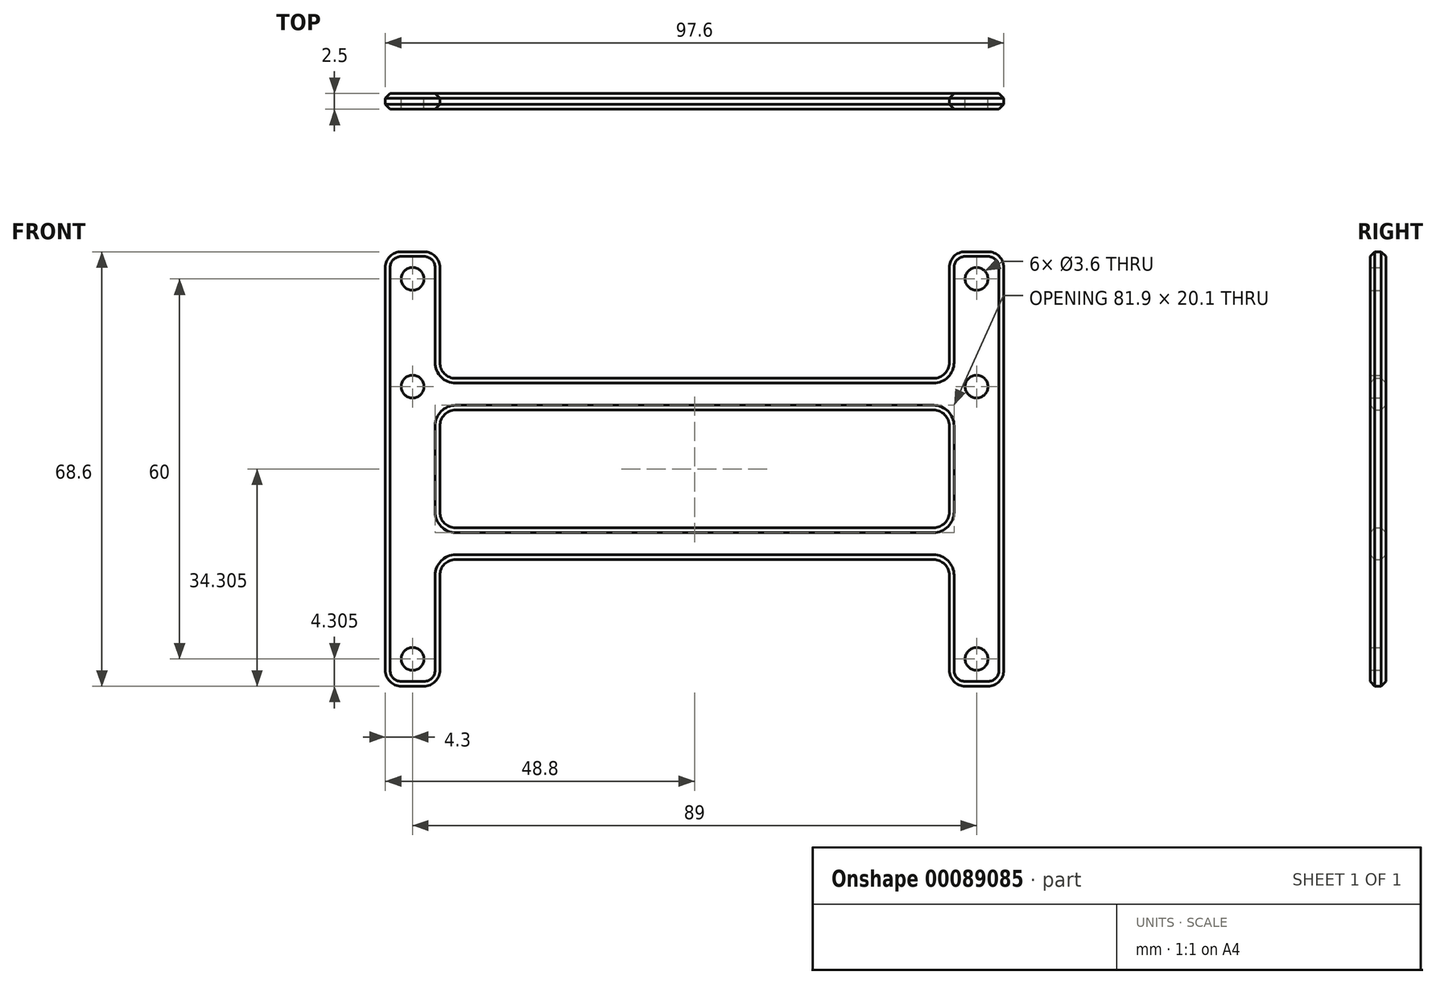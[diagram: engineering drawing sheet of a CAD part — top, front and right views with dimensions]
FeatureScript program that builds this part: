
annotation { "Feature Type Name" : "Feature", "Feature Type Description" : "" }
export const myFeature = defineFeature(function(context is Context, id is Id, definition is map)
    precondition{}
    {
        {
            var Q0;
            Q0=qCreatedBy(makeId("Front.planeOp"),FACE);
            var sketch = newSketch(context, id + "F0", { "sketchPlane" : qUnion([Q0])});
            skLineSegment(sketch, "E0.bottom", {"start": v(-48.8, 64.62) * mm, "end": v(-40.2, 64.62) * mm});
            skLineSegment(sketch, "E0.top", {"start": v(-48.8, -3.98) * mm, "end": v(-40.2, -3.98) * mm});
            skLineSegment(sketch, "E0.left", {"start": v(-48.8, 64.62) * mm, "end": v(-48.8, -3.98) * mm});
            skLineSegment(sketch, "E1", {"start": v(-44.5, 64.62) * mm, "end": v(-44.5, -55.68) * mm, "construction": true});
            skCircle(sketch, "E2", {"center": v(-44.5, 60.32) * mm, "radius": 1.8 * mm});
            skCircle(sketch, "E3", {"center": v(-44.5, 43.33) * mm, "radius": 1.8 * mm});
            skCircle(sketch, "E4", {"center": v(-44.5, 0.32) * mm, "radius": 1.8 * mm});
            skLineSegment(sketch, "E5", {"start": v(-40.2, 64.62) * mm, "end": v(-40.2, -3.98) * mm});
            skLineSegment(sketch, "E6.bottom", {"start": v(-40.2, 44.62) * mm, "end": v(0, 44.62) * mm});
            skLineSegment(sketch, "E6.top", {"start": v(-40.2, 39.62) * mm, "end": v(0, 39.62) * mm});
            skLineSegment(sketch, "E6.left", {"start": v(-40.2, 44.62) * mm, "end": v(-40.2, 39.62) * mm});
            skLineSegment(sketch, "E6.right", {"start": v(0, 44.62) * mm, "end": v(0, 39.62) * mm});
            skLineSegment(sketch, "E7.bottom", {"start": v(-40.23, 21.03) * mm, "end": v(0, 21.02) * mm});
            skLineSegment(sketch, "E7.top", {"start": v(-40.23, 16.03) * mm, "end": v(0, 16.02) * mm});
            skLineSegment(sketch, "E7.left", {"start": v(-40.23, 21.03) * mm, "end": v(-40.23, 16.02) * mm});
            skLineSegment(sketch, "E7.right", {"start": v(0, 21.02) * mm, "end": v(0, 16.02) * mm});
            skLineSegment(sketch, "E8.MirrorCS", {"start": v(40.23, 21.03) * mm, "end": v(40.23, 16.02) * mm});
            skCircle(sketch, "E9.MirrorC", {"center": v(44.5, 43.33) * mm, "radius": 1.8 * mm});
            skLineSegment(sketch, "E10.MirrorCS", {"start": v(40.2, 44.62) * mm, "end": v(40.2, 39.62) * mm});
            skLineSegment(sketch, "E11.MirrorCS", {"start": v(40.23, 16.02) * mm, "end": v(0, 16.02) * mm});
            skLineSegment(sketch, "E12.MirrorCS", {"start": v(40.23, 21.02) * mm, "end": v(0, 21.02) * mm});
            skCircle(sketch, "E13.MirrorC", {"center": v(44.5, 0.32) * mm, "radius": 1.8 * mm});
            skCircle(sketch, "E14.MirrorC", {"center": v(44.5, 60.32) * mm, "radius": 1.8 * mm});
            skLineSegment(sketch, "E15.MirrorCS", {"start": v(40.2, 39.62) * mm, "end": v(0, 39.62) * mm});
            skLineSegment(sketch, "E16.MirrorCS", {"start": v(48.8, 64.62) * mm, "end": v(48.8, -3.98) * mm});
            skLineSegment(sketch, "E17.MirrorCS", {"start": v(48.8, -3.98) * mm, "end": v(40.2, -3.98) * mm});
            skLineSegment(sketch, "E18.MirrorCS", {"start": v(40.2, 64.62) * mm, "end": v(40.2, -3.97) * mm});
            skLineSegment(sketch, "E19.MirrorCS", {"start": v(48.8, 64.62) * mm, "end": v(40.2, 64.62) * mm});
            skLineSegment(sketch, "E20.MirrorCS", {"start": v(40.2, 44.62) * mm, "end": v(0, 44.62) * mm});
            skSolve(sketch);
        }
        {
            var Q0;
            {var subQ5=sQuery(id+"F0.wireOp",EDGE,"E7.left");Q0=makeQuery(id+"F0.imprint","IMPRINT",FACE,{"disambiguationData":[TD([[makeQuery(id+"F0.imprint","IMPRINT",EDGE,{"derivedFrom":subQ5}),1.0]])]});}
            var Q1;
            {var subQ0=sQuery(id+"F0.wireOp",EDGE,"E8.MirrorCS");Q1=makeQuery(id+"F0.imprint","IMPRINT",FACE,{"disambiguationData":[TD([[makeQuery(id+"F0.imprint","IMPRINT",EDGE,{"derivedFrom":subQ0}),-1.0]])]});}
            var Q2;
            {var subQ5=sQuery(id+"F0.wireOp",EDGE,"E7.right");Q2=makeQuery(id+"F0.imprint","IMPRINT",FACE,{"disambiguationData":[TD([[makeQuery(id+"F0.imprint","IMPRINT",EDGE,{"derivedFrom":subQ5}),-1.0]])]});}
            var Q3;
            {var subQ0=sQuery(id+"F0.wireOp",EDGE,"E7.right");Q3=makeQuery(id+"F0.imprint","IMPRINT",FACE,{"disambiguationData":[TD([[makeQuery(id+"F0.imprint","IMPRINT",EDGE,{"derivedFrom":subQ0}),1.0]])]});}
            var Q4;
            {var subQ0=sQuery(id+"F0.wireOp",EDGE,"E15.MirrorCS");Q4=makeQuery(id+"F0.imprint","IMPRINT",FACE,{"disambiguationData":[TD([[makeQuery(id+"F0.imprint","IMPRINT",EDGE,{"derivedFrom":subQ0}),-1.0]])]});}
            var Q5;
            {var subQ9=sQuery(id+"F0.wireOp",EDGE,"E8.MirrorCS");Q5=makeQuery(id+"F0.imprint","IMPRINT",FACE,{"disambiguationData":[TD([[makeQuery(id+"F0.imprint","IMPRINT",EDGE,{"derivedFrom":subQ9}),1.0]])]});}
            var Q6;
            Q6=makeQuery(id+"F0.imprint","IMPRINT",FACE,{"disambiguationData":[TD([[makeQuery(id+"F0.imprint","IMPRINT",EDGE,{"derivedFrom":sQuery(id+"F0.wireOp",EDGE,"E6.bottom")}),-1.0]])]});
            var Q7;
            Q7=makeQuery(id+"F0.imprint","IMPRINT",FACE,{"disambiguationData":[TD([[makeQuery(id+"F0.imprint","IMPRINT",EDGE,{"derivedFrom":sQuery(id+"F0.wireOp",EDGE,"6060c022-7060-453b-8efb-dcd9e4211910.sketch_text.stroke-0")}),-1.0]])]});
            var Q8;
            Q8=makeQuery(id+"F0.imprint","IMPRINT",FACE,{"disambiguationData":[TD([[makeQuery(id+"F0.imprint","IMPRINT",EDGE,{"derivedFrom":sQuery(id+"F0.wireOp",EDGE,"6060c022-7060-453b-8efb-dcd9e4211910.sketch_text.stroke-80")}),-1.0]])]});
            var Q9;
            Q9=makeQuery(id+"F0.imprint","IMPRINT",FACE,{"disambiguationData":[TD([[makeQuery(id+"F0.imprint","IMPRINT",EDGE,{"derivedFrom":sQuery(id+"F0.wireOp",EDGE,"6060c022-7060-453b-8efb-dcd9e4211910.sketch_text.stroke-109")}),1.0]])]});
            var Q10;
            Q10=makeQuery(id+"F0.imprint","IMPRINT",FACE,{"disambiguationData":[TD([[makeQuery(id+"F0.imprint","IMPRINT",EDGE,{"derivedFrom":sQuery(id+"F0.wireOp",EDGE,"6060c022-7060-453b-8efb-dcd9e4211910.sketch_text.stroke-75")}),1.0]])]});
            var Q11;
            Q11=makeQuery(id+"F0.imprint","IMPRINT",FACE,{"disambiguationData":[TD([[makeQuery(id+"F0.imprint","IMPRINT",EDGE,{"derivedFrom":sQuery(id+"F0.wireOp",EDGE,"6060c022-7060-453b-8efb-dcd9e4211910.sketch_text.stroke-56")}),1.0]])]});
            var Q12;
            Q12=makeQuery(id+"F0.imprint","IMPRINT",FACE,{"disambiguationData":[TD([[makeQuery(id+"F0.imprint","IMPRINT",EDGE,{"derivedFrom":sQuery(id+"F0.wireOp",EDGE,"6060c022-7060-453b-8efb-dcd9e4211910.sketch_text.stroke-23")}),-1.0]])]});
            var Q13;
            Q13=makeQuery(id+"F0.imprint","IMPRINT",FACE,{"disambiguationData":[TD([[makeQuery(id+"F0.imprint","IMPRINT",EDGE,{"derivedFrom":sQuery(id+"F0.wireOp",EDGE,"6060c022-7060-453b-8efb-dcd9e4211910.sketch_text.stroke-13")}),-1.0]])]});
            var Q14;
            Q14=makeQuery(id+"F0.imprint","IMPRINT",FACE,{"disambiguationData":[TD([[makeQuery(id+"F0.imprint","IMPRINT",EDGE,{"derivedFrom":sQuery(id+"F0.wireOp",EDGE,"6060c022-7060-453b-8efb-dcd9e4211910.sketch_text.stroke-8")}),1.0]])]});
            var Q15;
            Q15=makeQuery(id+"F0.imprint","IMPRINT",FACE,{"disambiguationData":[TD([[makeQuery(id+"F0.imprint","IMPRINT",EDGE,{"derivedFrom":sQuery(id+"F0.wireOp",EDGE,"6060c022-7060-453b-8efb-dcd9e4211910.sketch_text.stroke-118")}),1.0]])]});
            var Q16;
            Q16=makeQuery(id+"F0.imprint","IMPRINT",FACE,{"disambiguationData":[TD([[makeQuery(id+"F0.imprint","IMPRINT",EDGE,{"derivedFrom":sQuery(id+"F0.wireOp",EDGE,"6060c022-7060-453b-8efb-dcd9e4211910.sketch_text.stroke-136")}),-1.0]])]});
            var Q17;
            Q17=makeQuery(id+"F0.imprint","IMPRINT",FACE,{"disambiguationData":[TD([[makeQuery(id+"F0.imprint","IMPRINT",EDGE,{"derivedFrom":sQuery(id+"F0.wireOp",EDGE,"6060c022-7060-453b-8efb-dcd9e4211910.sketch_text.stroke-124")}),-1.0]])]});
            var Q18;
            Q18=makeQuery(id+"F0.imprint","IMPRINT",FACE,{"disambiguationData":[TD([[makeQuery(id+"F0.imprint","IMPRINT",EDGE,{"derivedFrom":sQuery(id+"F0.wireOp",EDGE,"6060c022-7060-453b-8efb-dcd9e4211910.sketch_text.stroke-42")}),-1.0]])]});
            var Q19;
            Q19=makeQuery(id+"F0.imprint","IMPRINT",FACE,{"disambiguationData":[TD([[makeQuery(id+"F0.imprint","IMPRINT",EDGE,{"derivedFrom":sQuery(id+"F0.wireOp",EDGE,"6060c022-7060-453b-8efb-dcd9e4211910.sketch_text.stroke-187")}),-1.0]])]});
            var Q20;
            Q20=makeQuery(id+"F0.imprint","IMPRINT",FACE,{"disambiguationData":[TD([[makeQuery(id+"F0.imprint","IMPRINT",EDGE,{"derivedFrom":sQuery(id+"F0.wireOp",EDGE,"6060c022-7060-453b-8efb-dcd9e4211910.sketch_text.stroke-61")}),-1.0]])]});
            var Q21;
            {var subQ4=sQuery(id+"F0.wireOp",EDGE,"E0.bottom");Q21=makeQuery(id+"F0.imprint","IMPRINT",FACE,{"disambiguationData":[TD([[makeQuery(id+"F0.imprint","IMPRINT",EDGE,{"derivedFrom":subQ4}),-1.0]])]});}
            var Q22;
            Q22=makeQuery(id+"F0.imprint","IMPRINT",FACE,{"disambiguationData":[TD([[makeQuery(id+"F0.imprint","IMPRINT",EDGE,{"derivedFrom":sQuery(id+"F0.wireOp",EDGE,"6060c022-7060-453b-8efb-dcd9e4211910.sketch_text.stroke-195")}),-1.0]])]});
            var Q23;
            Q23=makeQuery(id+"F0.imprint","IMPRINT",FACE,{"disambiguationData":[TD([[makeQuery(id+"F0.imprint","IMPRINT",EDGE,{"derivedFrom":sQuery(id+"F0.wireOp",EDGE,"6060c022-7060-453b-8efb-dcd9e4211910.sketch_text.stroke-155")}),-1.0]])]});
            var Q24;
            Q24=makeQuery(id+"F0.imprint","IMPRINT",FACE,{"disambiguationData":[TD([[makeQuery(id+"F0.imprint","IMPRINT",EDGE,{"derivedFrom":sQuery(id+"F0.wireOp",EDGE,"6060c022-7060-453b-8efb-dcd9e4211910.sketch_text.stroke-234")}),-1.0]])]});
            var Q25;
            Q25=makeQuery(id+"F0.imprint","IMPRINT",FACE,{"disambiguationData":[TD([[makeQuery(id+"F0.imprint","IMPRINT",EDGE,{"derivedFrom":sQuery(id+"F0.wireOp",EDGE,"6060c022-7060-453b-8efb-dcd9e4211910.sketch_text.stroke-224")}),-1.0]])]});
            var Q26;
            Q26=makeQuery(id+"F0.imprint","IMPRINT",FACE,{"disambiguationData":[TD([[makeQuery(id+"F0.imprint","IMPRINT",EDGE,{"derivedFrom":sQuery(id+"F0.wireOp",EDGE,"6060c022-7060-453b-8efb-dcd9e4211910.sketch_text.stroke-212")}),-1.0]])]});
            var Q27;
            Q27=makeQuery(id+"F0.imprint","IMPRINT",FACE,{"disambiguationData":[TD([[makeQuery(id+"F0.imprint","IMPRINT",EDGE,{"derivedFrom":sQuery(id+"F0.wireOp",EDGE,"6060c022-7060-453b-8efb-dcd9e4211910.sketch_text.stroke-216")}),-1.0]])]});
            var Q28;
            Q28=makeQuery(id+"F0.imprint","IMPRINT",FACE,{"disambiguationData":[TD([[makeQuery(id+"F0.imprint","IMPRINT",EDGE,{"derivedFrom":sQuery(id+"F0.wireOp",EDGE,"6060c022-7060-453b-8efb-dcd9e4211910.sketch_text.stroke-183")}),-1.0]])]});
            var Q29;
            Q29=qSketchRegion(id+"F0",true);
            extrude(context, id + "F1", {"entities" : qUnion([Q0, Q1, Q2, Q3, Q4, Q5, Q6, Q7, Q8, Q9, Q10, Q11, Q12, Q13, Q14, Q15, Q16, Q17, Q18, Q19, Q20, Q21, Q22, Q23, Q24, Q25, Q26, Q27, Q28, Q29]), "depth" : 2.5 * mm});
        }
        {
            var Q0;
            Q0=makeQuery(id+"F1.opExtrude","SWEPT_EDGE",EDGE,{"disambiguationData":[OSD([sQuery(id+"F0.wireOp",EDGE,"E5"),sQuery(id+"F0.wireOp",EDGE,"E6.bottom"),sQuery(id+"F0.wireOp",EDGE,"E6.left")])]});
            var Q1;
            Q1=makeQuery(id+"F1.opExtrude","SWEPT_EDGE",EDGE,{"disambiguationData":[OSD([sQuery(id+"F0.wireOp",EDGE,"E18.MirrorCS"),sQuery(id+"F0.wireOp",EDGE,"E20.MirrorCS")])]});
            var Q2;
            Q2=makeQuery(id+"F1.opExtrude","SWEPT_EDGE",EDGE,{"disambiguationData":[OSD([sQuery(id+"F0.wireOp",EDGE,"E5"),sQuery(id+"F0.wireOp",EDGE,"E6.top"),sQuery(id+"F0.wireOp",EDGE,"E6.left")])]});
            var Q3;
            Q3=makeQuery(id+"F1.opExtrude","SWEPT_EDGE",EDGE,{"disambiguationData":[OSD([sQuery(id+"F0.wireOp",EDGE,"E15.MirrorCS"),sQuery(id+"F0.wireOp",EDGE,"E18.MirrorCS")])]});
            var Q4;
            Q4=makeQuery(id+"F1.opExtrude","SWEPT_EDGE",EDGE,{"disambiguationData":[OSD([sQuery(id+"F0.wireOp",EDGE,"E5"),sQuery(id+"F0.wireOp",EDGE,"E7.bottom")])]});
            var Q5;
            Q5=makeQuery(id+"F1.opExtrude","SWEPT_EDGE",EDGE,{"disambiguationData":[OSD([sQuery(id+"F0.wireOp",EDGE,"E12.MirrorCS"),sQuery(id+"F0.wireOp",EDGE,"E18.MirrorCS")])]});
            var Q6;
            Q6=makeQuery(id+"F1.opExtrude","SWEPT_EDGE",EDGE,{"disambiguationData":[OSD([sQuery(id+"F0.wireOp",EDGE,"E5"),sQuery(id+"F0.wireOp",EDGE,"E7.top")])]});
            var Q7;
            Q7=makeQuery(id+"F1.opExtrude","SWEPT_EDGE",EDGE,{"disambiguationData":[OSD([sQuery(id+"F0.wireOp",EDGE,"E11.MirrorCS"),sQuery(id+"F0.wireOp",EDGE,"E18.MirrorCS")])]});
            var Q8;
            Q8=makeQuery(id+"F1.opExtrude","SWEPT_EDGE",EDGE,{"disambiguationData":[OSD([sQuery(id+"F0.wireOp",EDGE,"E17.MirrorCS"),sQuery(id+"F0.wireOp",EDGE,"E18.MirrorCS")])]});
            var Q9;
            Q9=makeQuery(id+"F1.opExtrude","SWEPT_EDGE",EDGE,{"disambiguationData":[OSD([sQuery(id+"F0.wireOp",EDGE,"E16.MirrorCS"),sQuery(id+"F0.wireOp",EDGE,"E17.MirrorCS")])]});
            var Q10;
            Q10=makeQuery(id+"F1.opExtrude","SWEPT_EDGE",EDGE,{"disambiguationData":[OSD([sQuery(id+"F0.wireOp",EDGE,"E0.top"),sQuery(id+"F0.wireOp",EDGE,"E0.left")])]});
            var Q11;
            Q11=makeQuery(id+"F1.opExtrude","SWEPT_EDGE",EDGE,{"disambiguationData":[OSD([sQuery(id+"F0.wireOp",EDGE,"E0.top"),sQuery(id+"F0.wireOp",EDGE,"E5")])]});
            var Q12;
            Q12=makeQuery(id+"F1.opExtrude","SWEPT_EDGE",EDGE,{"disambiguationData":[OSD([sQuery(id+"F0.wireOp",EDGE,"E16.MirrorCS"),sQuery(id+"F0.wireOp",EDGE,"E19.MirrorCS")])]});
            var Q13;
            Q13=makeQuery(id+"F1.opExtrude","SWEPT_EDGE",EDGE,{"disambiguationData":[OSD([sQuery(id+"F0.wireOp",EDGE,"E18.MirrorCS"),sQuery(id+"F0.wireOp",EDGE,"E19.MirrorCS")])]});
            var Q14;
            Q14=makeQuery(id+"F1.opExtrude","SWEPT_EDGE",EDGE,{"disambiguationData":[OSD([sQuery(id+"F0.wireOp",EDGE,"E0.bottom"),sQuery(id+"F0.wireOp",EDGE,"E0.left")])]});
            var Q15;
            Q15=makeQuery(id+"F1.opExtrude","SWEPT_EDGE",EDGE,{"disambiguationData":[OSD([sQuery(id+"F0.wireOp",EDGE,"E0.bottom"),sQuery(id+"F0.wireOp",EDGE,"E5")])]});
            fillet(context, id + "F2", {"entities" : qUnion([Q0, Q1, Q2, Q3, Q4, Q5, Q6, Q7, Q8, Q9, Q10, Q11, Q12, Q13, Q14, Q15]), "radius" : 2.5 * mm, "tangentPropagation" : true, "allowEdgeOverflow" : false});
        }
        {
            var Q0;
            Q0=makeQuery(id+"F1.opExtrude","CAP_EDGE",EDGE,{"disambiguationData":[OSD([sQuery(id+"F0.wireOp",EDGE,"E7.top"),sQuery(id+"F0.wireOp",EDGE,"E11.MirrorCS")])],"isStart":true});
            var Q1;
            Q1=makeQuery(id+"F1.opExtrude","CAP_EDGE",EDGE,{"disambiguationData":[OSD([sQuery(id+"F0.wireOp",EDGE,"E6.top"),sQuery(id+"F0.wireOp",EDGE,"E15.MirrorCS")])],"isStart":true});
            var Q2;
            Q2=makeQuery(id+"F1.opExtrude","CAP_EDGE",EDGE,{"disambiguationData":[OSD([sQuery(id+"F0.wireOp",EDGE,"E0.bottom")])],"isStart":false});
            var Q3;
            Q3=makeQuery(id+"F1.opExtrude","CAP_EDGE",EDGE,{"disambiguationData":[OSD([sQuery(id+"F0.wireOp",EDGE,"E6.top"),sQuery(id+"F0.wireOp",EDGE,"E15.MirrorCS")])],"isStart":false});
            chamfer(context, id + "F3", {"entities" : qUnion([Q0, Q1, Q2, Q3]), "width" : .75 * mm, "tangentPropagation" : true});
        }
    });
